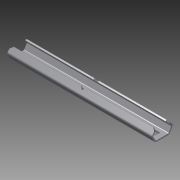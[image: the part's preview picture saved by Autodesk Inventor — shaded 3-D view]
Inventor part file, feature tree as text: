
AUTODESK INVENTOR PART (.ipt)
format: ipt  version: 2014 (Build 180170000, 170)  size: 370,688 bytes
history: native  units: in
note: dims shown in document units (in); Inventor stores cm internally (conversion verified against a paired STEP export)
features: other x1, imported_body x1, extrude x1, sketch x1
ambient origin geometry x8: Origin, YZ Plane, XZ Plane, XY Plane, X Axis, Y Axis, Z Axis, Center Point
bodies: Body1 (feature_tree)
feature tree (4):
  parser-record x1  (decoder bookkeeping rows leaked as tree rows — omitted from the tree; the rows remain in map.json)
  imported_body  "Base1"
  extrude  "Extrusion1"  Depth=1.0in TaperAngle=0.0deg
  sketch  "Sketch1"  dims[d0=5.0in d1=1.0in d2=0.0in]
